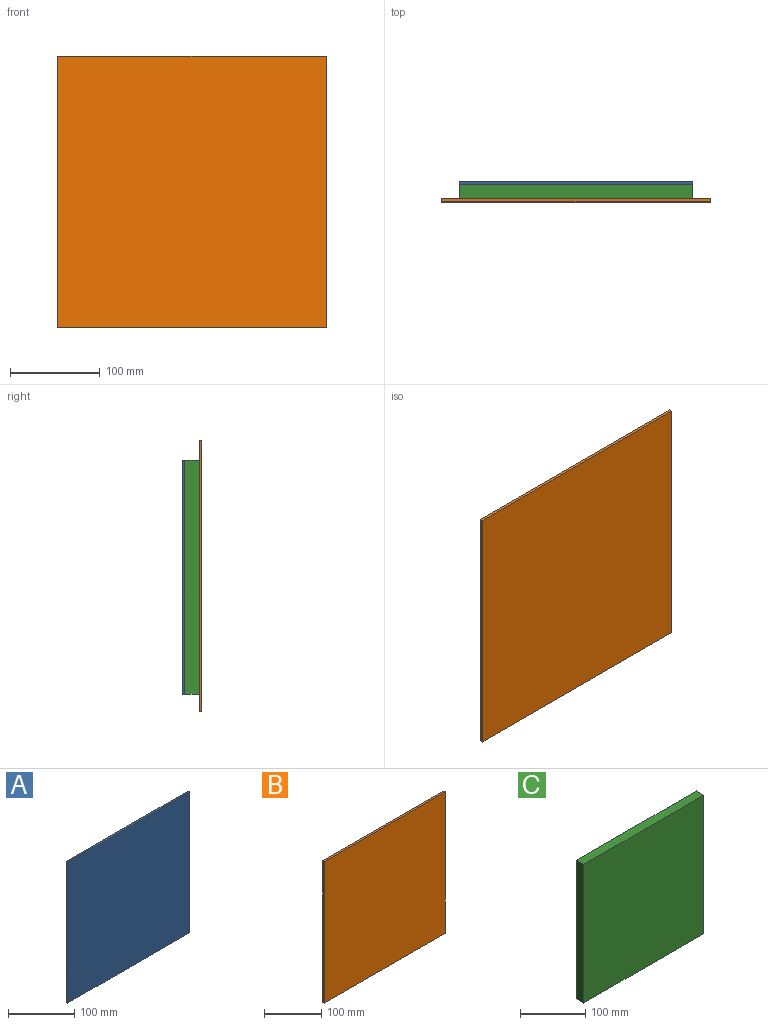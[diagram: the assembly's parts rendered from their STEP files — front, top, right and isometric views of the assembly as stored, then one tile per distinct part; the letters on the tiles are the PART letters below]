
ASSEMBLY  parts=3 mates=2
PART A: 6 faces, bbox 260.4x3.2x260.4 mm
  f0: plane 260.35x3.18mm, normal (0,0,-1), area 826.6mm2, adj f1,f3,f4,f5
  f1: plane 260.35x3.18mm, normal (1,0,0), area 826.6mm2, adj f0,f2,f4,f5
  f2: plane 260.35x3.18mm, normal (0,0,1), area 826.6mm2, adj f1,f3,f4,f5
  f3: plane 260.35x3.18mm, normal (-1,0,0), area 826.6mm2, adj f0,f2,f4,f5
  f4: plane 260.35x260.35mm, normal (0,-1,0), area 67782.1mm2, adj f0,f1,f2,f3
  f5: plane 260.35x260.35mm, normal (0,1,0), area 67782.1mm2, adj f0,f1,f2,f3
PART B: 6 faces, bbox 298.5x3.2x301.6 mm
  f0: plane 298.45x3.18mm, normal (0,0,-1), area 947.6mm2, adj f1,f3,f4,f5
  f1: plane 301.63x3.18mm, normal (1,0,0), area 957.7mm2, adj f0,f2,f4,f5
  f2: plane 298.45x3.18mm, normal (0,0,1), area 947.6mm2, adj f1,f3,f4,f5
  f3: plane 301.63x3.18mm, normal (-1,0,0), area 957.7mm2, adj f0,f2,f4,f5
  f4: plane 301.63x298.45mm, normal (0,-1,0), area 90020mm2, adj f0,f1,f2,f3
  f5: plane 301.63x298.45mm, normal (0,1,0), area 90020mm2, adj f0,f1,f2,f3
PART C: 6 faces, bbox 260.4x15.9x260.4 mm
  f0: plane 260.35x15.88mm, normal (0,0,-1), area 4133.1mm2, adj f1,f3,f4,f5
  f1: plane 260.35x15.88mm, normal (1,0,0), area 4133.1mm2, adj f0,f2,f4,f5
  f2: plane 260.35x15.88mm, normal (0,0,1), area 4133.1mm2, adj f1,f3,f4,f5
  f3: plane 260.35x15.88mm, normal (-1,0,0), area 4133.1mm2, adj f0,f2,f4,f5
  f4: plane 260.35x260.35mm, normal (0,-1,0), area 67782.1mm2, adj f0,f1,f2,f3
  f5: plane 260.35x260.35mm, normal (0,1,0), area 67782.1mm2, adj f0,f1,f2,f3
PLACE A t=(106.27,27.29,-487.46)mm
PLACE B t=(106.27,8.24,-485.88)mm
PLACE C t=(106.27,24.11,-958.08)mm
MATE fastened B.f5 <-> C.f4  axis (0,1,0) through (106.27,8.24,1.59)mm
MATE fastened C.f5 <-> A.f4  axis (0,1,0) through (106.27,24.11,0)mm
